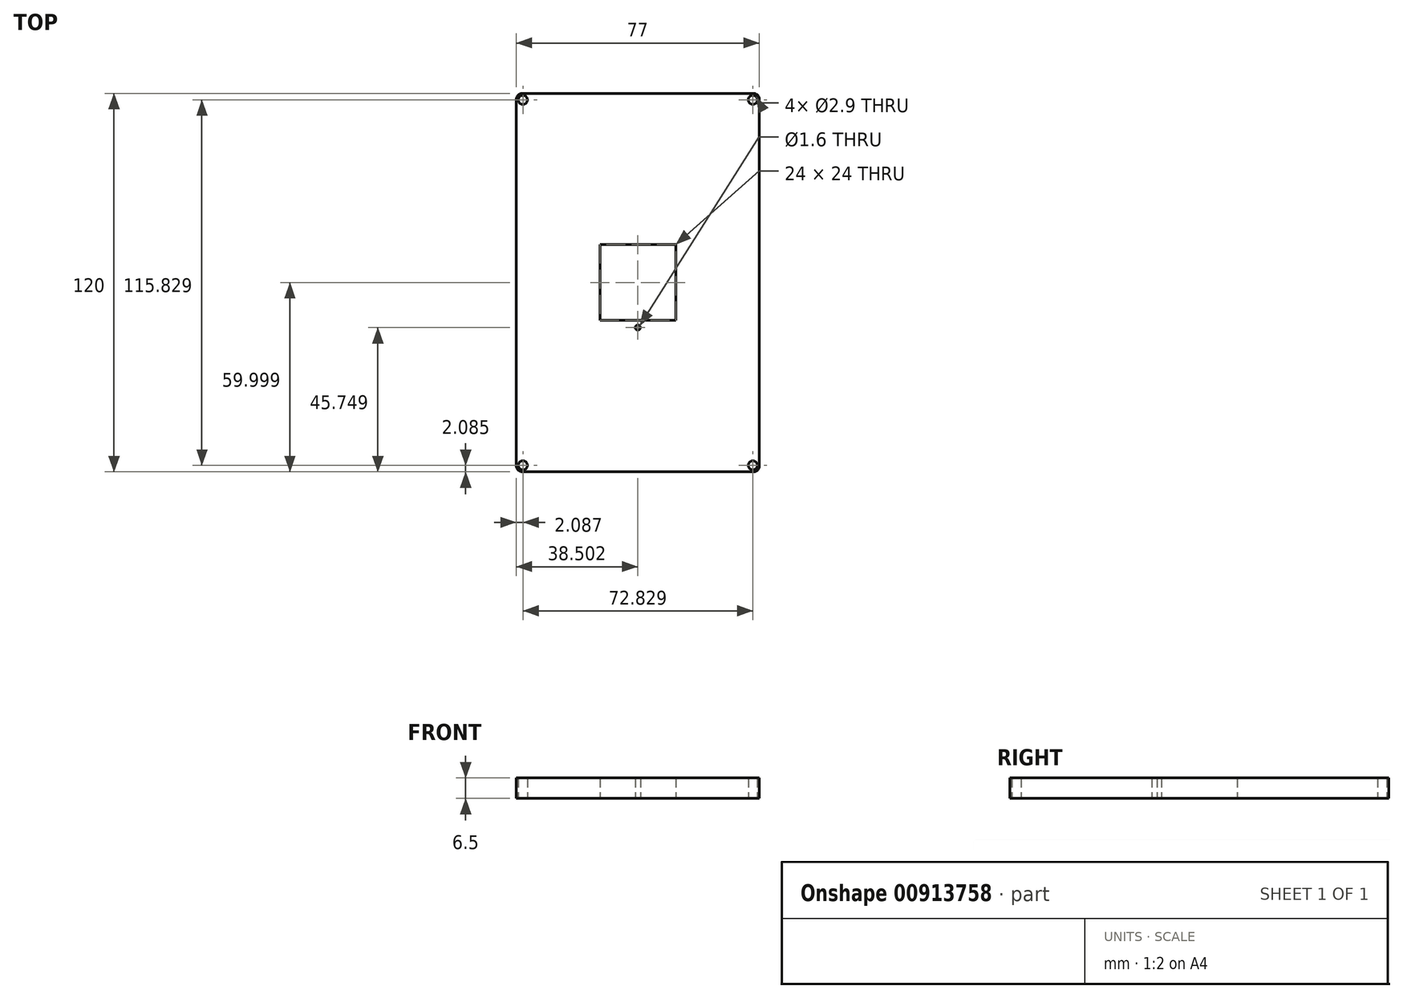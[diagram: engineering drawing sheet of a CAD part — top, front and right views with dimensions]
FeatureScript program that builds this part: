
annotation { "Feature Type Name" : "Feature", "Feature Type Description" : "" }
export const myFeature = defineFeature(function(context is Context, id is Id, definition is map)
    precondition{}
    {
        {
            var Q0;
            Q0=qCreatedBy(makeId("Top.planeOp"),FACE);
            var sketch = newSketch(context, id + "F0", { "sketchPlane" : qUnion([Q0])});
            skLineSegment(sketch, "E0.bottom", {"start": v(-34.17, 31.85) * mm, "end": v(38.83, 31.85) * mm});
            skLineSegment(sketch, "E0.top", {"start": v(-34.17, -88.15) * mm, "end": v(38.83, -88.15) * mm});
            skLineSegment(sketch, "E0.left", {"start": v(-36.17, 29.85) * mm, "end": v(-36.17, -86.15) * mm});
            skLineSegment(sketch, "E0.right", {"start": v(40.83, 29.85) * mm, "end": v(40.83, -86.15) * mm});
            skLineSegment(sketch, "E1", {"start": v(2.33, 31.85) * mm, "end": v(2.33, -88.15) * mm, "construction": true});
            skLineSegment(sketch, "E2", {"start": v(-36.17, -28.15) * mm, "end": v(40.83, -28.15) * mm, "construction": true});
            skPoint(sketch, "E3.visualSharp", {"position": v(-36.17, 31.85) * mm});
            skArc(sketch, "E3.filletArc", {"start": v(-34.17, 31.85) * mm, "mid": v(-35.58, 31.26) * mm, "end": v(-36.17, 29.85) * mm});
            skPoint(sketch, "E4.visualSharp", {"position": v(40.83, 31.85) * mm});
            skArc(sketch, "E4.filletArc", {"start": v(40.83, 29.85) * mm, "mid": v(40.25, 31.26) * mm, "end": v(38.83, 31.85) * mm});
            skPoint(sketch, "E5.visualSharp", {"position": v(40.83, -88.15) * mm});
            skArc(sketch, "E5.filletArc", {"start": v(38.83, -88.15) * mm, "mid": v(40.25, -87.56) * mm, "end": v(40.83, -86.15) * mm});
            skPoint(sketch, "E6.visualSharp", {"position": v(-36.17, -88.15) * mm});
            skArc(sketch, "E6.filletArc", {"start": v(-36.17, -86.15) * mm, "mid": v(-35.58, -87.56) * mm, "end": v(-34.17, -88.15) * mm});
            skLineSegment(sketch, "E7", {"start": v(2.33, 31.85) * mm, "end": v(-34.17, 31.85) * mm});
            skLineSegment(sketch, "E8", {"start": v(-36.17, 29.85) * mm, "end": v(-36.17, -28.15) * mm});
            skLineSegment(sketch, "E9.bottom", {"start": v(-9.67, -16.15) * mm, "end": v(14.33, -16.15) * mm});
            skLineSegment(sketch, "E9.top", {"start": v(-9.67, -40.15) * mm, "end": v(14.33, -40.15) * mm});
            skLineSegment(sketch, "E9.left", {"start": v(-9.67, -16.15) * mm, "end": v(-9.67, -40.15) * mm});
            skLineSegment(sketch, "E9.right", {"start": v(14.33, -16.15) * mm, "end": v(14.33, -40.15) * mm});
            skCircle(sketch, "E10", {"center": v(2.33, -13.9) * mm, "radius": 0.8 * mm});
            skCircle(sketch, "E11.MirrorC", {"center": v(2.33, -42.4) * mm, "radius": 0.8 * mm});
            skLineSegment(sketch, "E12", {"start": v(-35.58, 31.26) * mm, "end": v(-31.45, 27.13) * mm, "construction": true});
            skCircle(sketch, "E13", {"center": v(-34.08, 29.76) * mm, "radius": 1.45 * mm});
            skCircle(sketch, "E14.MirrorC", {"center": v(38.75, 29.76) * mm, "radius": 1.45 * mm});
            skLineSegment(sketch, "E15.MirrorCS", {"start": v(40.83, -28.15) * mm, "end": v(-36.17, -28.15) * mm, "construction": true});
            skCircle(sketch, "E16.MirrorC", {"center": v(38.75, -86.07) * mm, "radius": 1.45 * mm});
            skCircle(sketch, "E17.MirrorC", {"center": v(-34.08, -86.07) * mm, "radius": 1.45 * mm});
            skSolve(sketch);
        }
        {
            var Q0;
            Q0=makeQuery(id+"F0.imprint","IMPRINT",FACE,{"disambiguationData":[TD([[makeQuery(id+"F0.imprint","IMPRINT",EDGE,{"derivedFrom":sQuery(id+"F0.wireOp",EDGE,"E0.bottom")}),-1.0]])]});
            extrude(context, id + "F1", {"entities" : qUnion([Q0]), "depth" : 3 * mm, "offsetDistance" : 25 * mm});
        }
        {
            var Q0;
            Q0=makeQuery(id+"F0.imprint","IMPRINT",FACE,{"disambiguationData":[TD([[makeQuery(id+"F0.imprint","IMPRINT",EDGE,{"derivedFrom":sQuery(id+"F0.wireOp",EDGE,"E10")}),1.0]])]});
            var Q1;
            Q1=makeQuery(id+"F0.imprint","IMPRINT",FACE,{"disambiguationData":[TD([[makeQuery(id+"F0.imprint","IMPRINT",EDGE,{"derivedFrom":sQuery(id+"F0.wireOp",EDGE,"E11.MirrorC")}),-1.0]])]});
            extrude(context, id + "F2", {"entities" : qUnion([Q0, Q1]), "operationType" : NewBodyOperationType.ADD, "depth" : 6.5 * mm, "offsetDistance" : 25 * mm});
        }
    });
